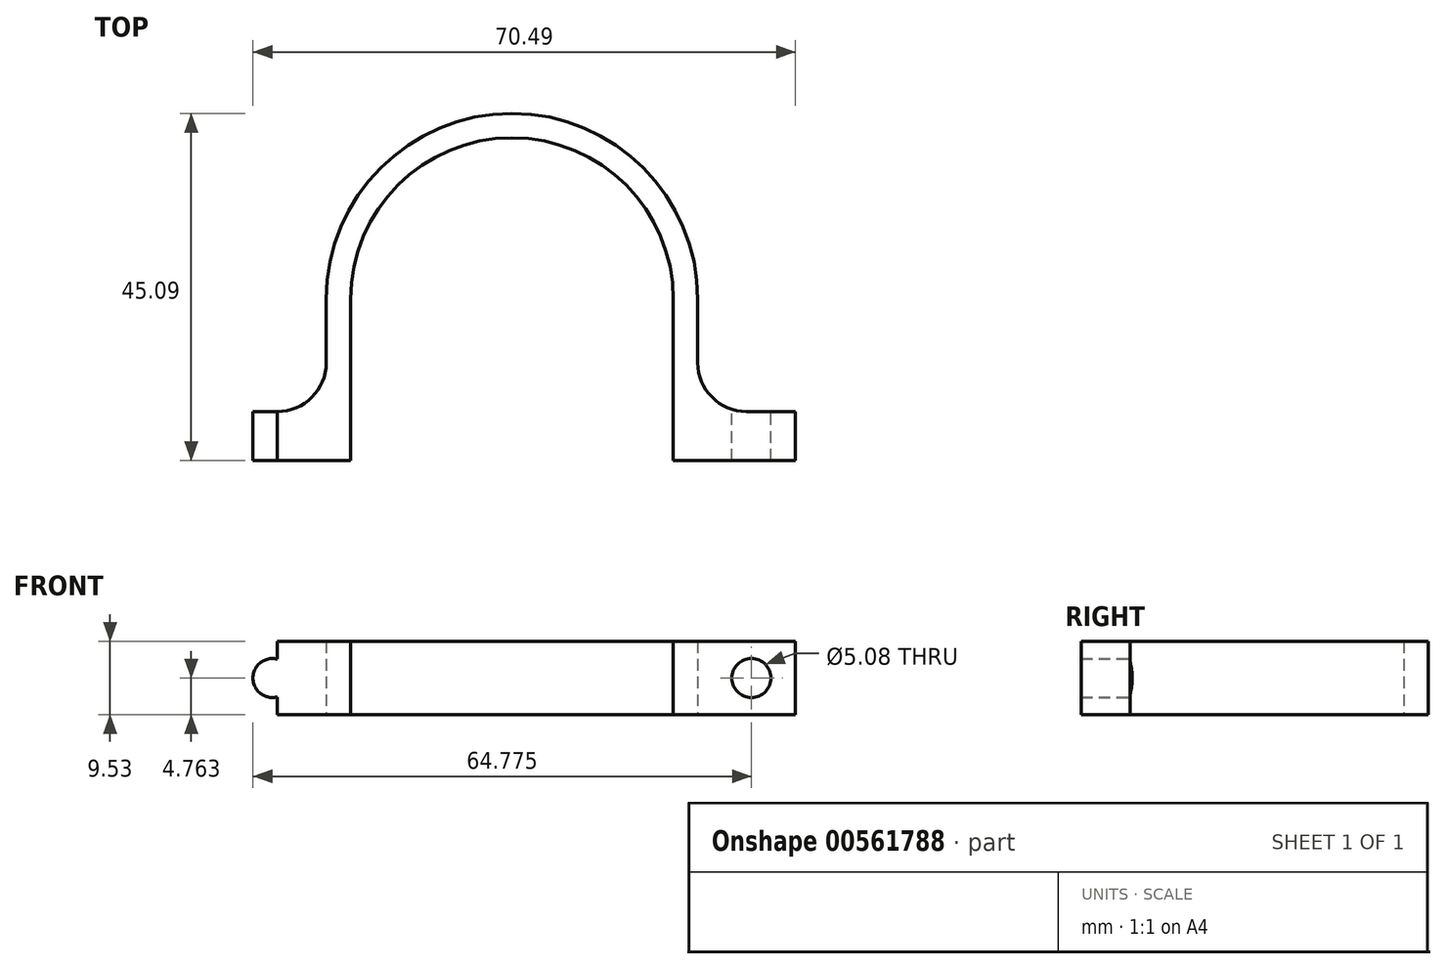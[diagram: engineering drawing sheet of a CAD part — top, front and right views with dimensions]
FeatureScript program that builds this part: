
annotation { "Feature Type Name" : "Feature", "Feature Type Description" : "" }
export const myFeature = defineFeature(function(context is Context, id is Id, definition is map)
    precondition{}
    {
        {
            var Q0;
            Q0=qCreatedBy(makeId("Top.planeOp"),FACE);
            var sketch = newSketch(context, id + "F0", { "sketchPlane" : qUnion([Q0])});
            skArc(sketch, "E0", {"start": v(0, 20.96) * mm, "mid": v(-14.82, 14.82) * mm, "end": v(-20.96, 0) * mm});
            skLineSegment(sketch, "E1", {"start": v(-20.96, -20.96) * mm, "end": v(-36.83, -20.96) * mm});
            skLineSegment(sketch, "E2", {"start": v(-20.96, 0) * mm, "end": v(-20.96, -20.96) * mm});
            skPoint(sketch, "E3.orphan", {"position": v(0, -20.96) * mm});
            skLineSegment(sketch, "E4", {"start": v(0, -30.1) * mm, "end": v(0, 38.63) * mm, "construction": true});
            skArc(sketch, "E5.0", {"start": v(0, 24.13) * mm, "mid": v(-17.06, 17.06) * mm, "end": v(-24.13, 0) * mm});
            skLineSegment(sketch, "E6.0", {"start": v(-24.13, 0) * mm, "end": v(-24.13, -8.26) * mm});
            skLineSegment(sketch, "E7.0", {"start": v(-30.48, -14.6) * mm, "end": v(-36.83, -14.6) * mm});
            skLineSegment(sketch, "E8", {"start": v(-36.83, -14.6) * mm, "end": v(-36.83, -20.96) * mm});
            skLineSegment(sketch, "E9.MirrorCS", {"start": v(36.83, -14.6) * mm, "end": v(36.83, -20.96) * mm});
            skLineSegment(sketch, "E10.MirrorCS", {"start": v(30.48, -14.6) * mm, "end": v(36.83, -14.6) * mm});
            skLineSegment(sketch, "E11.MirrorCS", {"start": v(24.13, 0) * mm, "end": v(24.13, -8.26) * mm});
            skLineSegment(sketch, "E12.MirrorCS", {"start": v(20.96, 0) * mm, "end": v(20.96, -20.96) * mm});
            skArc(sketch, "E13.MirrorCS", {"start": v(0, 20.96) * mm, "mid": v(14.82, 14.82) * mm, "end": v(20.96, 0) * mm});
            skArc(sketch, "E14.MirrorCS", {"start": v(0, 24.13) * mm, "mid": v(17.06, 17.06) * mm, "end": v(24.13, 0) * mm});
            skLineSegment(sketch, "E15.MirrorCS", {"start": v(20.96, -20.96) * mm, "end": v(36.83, -20.96) * mm});
            skPoint(sketch, "E16.visualSharp", {"position": v(-24.13, -14.6) * mm});
            skArc(sketch, "E16.filletArc", {"start": v(-30.48, -14.6) * mm, "mid": v(-25.99, -12.75) * mm, "end": v(-24.13, -8.26) * mm});
            skPoint(sketch, "E17.visualSharp", {"position": v(24.13, -14.6) * mm});
            skArc(sketch, "E17.filletArc", {"start": v(24.13, -8.26) * mm, "mid": v(25.99, -12.75) * mm, "end": v(30.48, -14.6) * mm});
            skSolve(sketch);
        }
        {
            var Q0;
            Q0=makeQuery(id+"F0.imprint","IMPRINT",FACE,{"disambiguationData":[TD([[makeQuery(id+"F0.imprint","IMPRINT",EDGE,{"derivedFrom":sQuery(id+"F0.wireOp",EDGE,"E0")}),-1.0]])]});
            extrude(context, id + "F1", {"entities" : qUnion([Q0]), "depth" : 9.52 * mm, "offsetDistance" : 25.4 * mm});
        }
        {
            var Q0;
            Q0=makeQuery(id+"F1.opExtrude","SWEPT_FACE",FACE,{"disambiguationData":[OSD([sQuery(id+"F0.wireOp",EDGE,"E7.0")])]});
            var sketch = newSketch(context, id + "F2", { "sketchPlane" : qUnion([Q0])});
            skCircle(sketch, "E18", {"center": v(-31.12, 4.76) * mm, "radius": 2.54 * mm});
            skLineSegment(sketch, "E19", {"start": v(-31.12, 4.76) * mm, "end": v(-47.9, 4.76) * mm, "construction": true});
            skCircle(sketch, "E20.MirrorC", {"center": v(31.12, 4.76) * mm, "radius": 2.54 * mm});
            skSolve(sketch);
        }
        {
            var Q0;
            Q0=makeQuery(id+"F2.imprint","IMPRINT",FACE,{"disambiguationData":[TD([[makeQuery(id+"F2.imprint","IMPRINT",EDGE,{"derivedFrom":sQuery(id+"F2.wireOp",EDGE,"E18")}),1.0]])]});
            var Q1;
            {var subQ0=sQuery(id+"F2.wireOp",EDGE,"E20.MirrorC");var subQ1=makeQuery(id+"F1.opExtrude","SWEPT_EDGE",EDGE,{"disambiguationData":[OSD([sQuery(id+"F0.wireOp",EDGE,"E7.0"),sQuery(id+"F0.wireOp",EDGE,"E16.filletArc")])]});var subQ2=makeQuery(id+"F2.imprint","INTERSECT",VERTEX,{"disambiguationData":[OD(0.0)],"derivedFrom":[subQ1,subQ0]});Q1=makeQuery(id+"F2.imprint","IMPRINT",FACE,{"disambiguationData":[TD([[makeQuery(id+"F2.imprint","IMPRINT",EDGE,{"disambiguationData":[TD([[subQ2,1.0]])],"derivedFrom":subQ0}),-1.0]])]});}
            var Q2;
            {var subQ0=sQuery(id+"F2.wireOp",EDGE,"E20.MirrorC");var subQ1=makeQuery(id+"F1.opExtrude","SWEPT_EDGE",EDGE,{"disambiguationData":[OSD([sQuery(id+"F0.wireOp",EDGE,"E7.0"),sQuery(id+"F0.wireOp",EDGE,"E16.filletArc")])]});var subQ2=makeQuery(id+"F2.imprint","INTERSECT",VERTEX,{"disambiguationData":[OD(0.0)],"derivedFrom":[subQ1,subQ0]});Q2=makeQuery(id+"F2.imprint","IMPRINT",FACE,{"disambiguationData":[TD([[makeQuery(id+"F2.imprint","IMPRINT",EDGE,{"disambiguationData":[TD([[subQ2,-1.0]])],"derivedFrom":subQ0}),-1.0]])]});}
            extrude(context, id + "F3", {"entities" : qUnion([Q0, Q1, Q2]), "operationType" : NewBodyOperationType.REMOVE, "oppositeDirection" : true, "depth" : 25.4 * mm, "offsetDistance" : 25.4 * mm, "hasSecondDirection" : true, "secondDirectionOppositeDirection" : false, "secondDirectionDepth" : 25.4 * mm});
        }
    });
